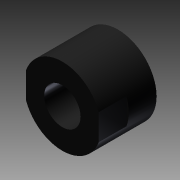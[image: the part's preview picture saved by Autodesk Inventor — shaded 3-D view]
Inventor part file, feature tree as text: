
AUTODESK INVENTOR PART (.ipt)
format: ipt  version: 2011 (Build 150239000, 239)  size: 88,064 bytes
history: native  units: in
note: dims shown in document units (in); Inventor stores cm internally (conversion verified against a paired STEP export)
features: extrude x2, sketch x2
ambient origin geometry x8: Origin, YZ Plane, XZ Plane, XY Plane, X Axis, Y Axis, Z Axis, Center Point
bodies: Solid1 (feature_tree)
feature tree (4):
  extrude  "Extrusion1"  Depth=0.903in
  extrude  "Extrusion2"  Depth=0.85in
  sketch  "Sketch1"  dims[d0=0.425in d1=0.903in]
  sketch  "Sketch2"  dims[d2=0.325in d3=0.0in d4=0.85in d5=0.325in d6=0.0in]
